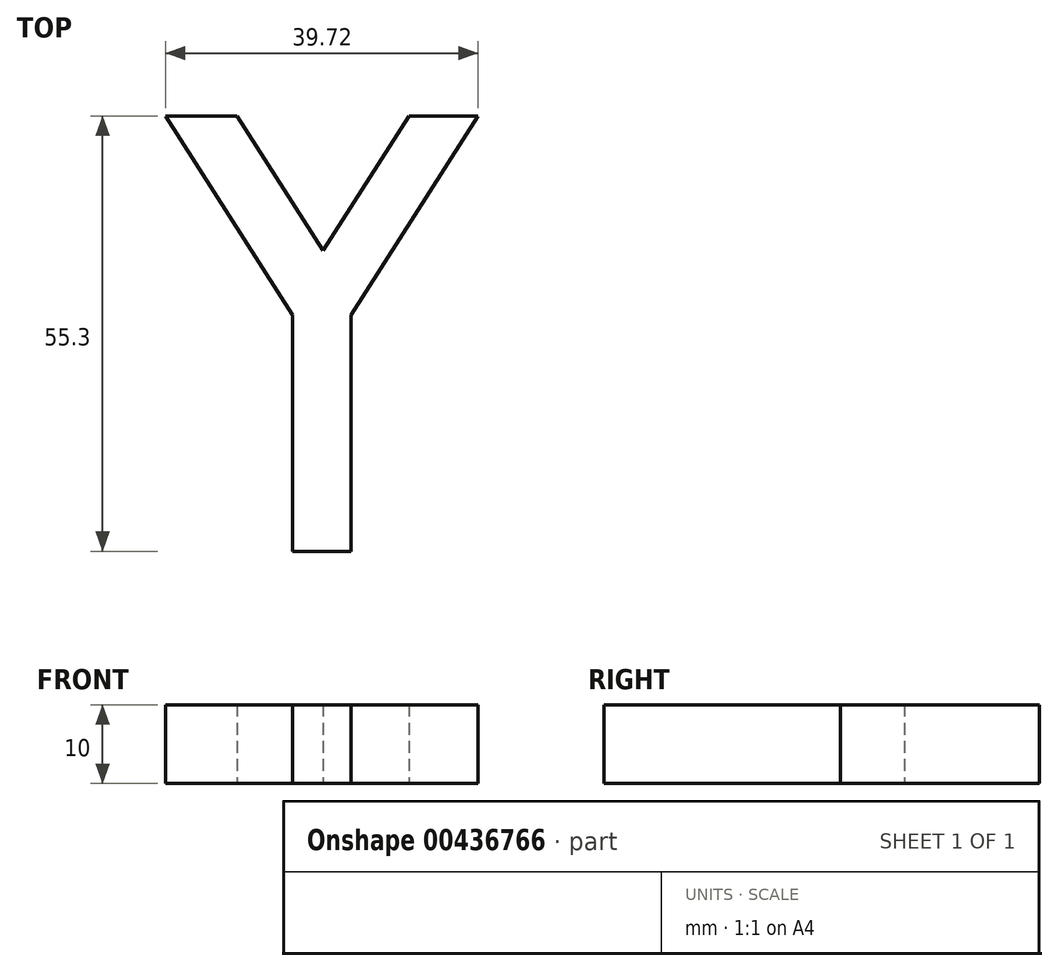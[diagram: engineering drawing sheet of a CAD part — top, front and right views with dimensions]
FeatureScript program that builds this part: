
annotation { "Feature Type Name" : "Feature", "Feature Type Description" : "" }
export const myFeature = defineFeature(function(context is Context, id is Id, definition is map)
    precondition{}
    {
        {
            var Q0;
            Q0=qCreatedBy(makeId("Top.planeOp"),FACE);
            var sketch = newSketch(context, id + "F0", { "sketchPlane" : qUnion([Q0])});
            skLineSegment(sketch, "E0", {"start": v(18.43, 27.61) * mm, "end": v(18.43, -2.39) * mm});
            skLineSegment(sketch, "E1", {"start": v(18.43, 27.61) * mm, "end": v(34.55, 52.91) * mm});
            skLineSegment(sketch, "E2", {"start": v(34.55, 52.91) * mm, "end": v(38.29, 52.91) * mm});
            skLineSegment(sketch, "E3", {"start": v(38.29, 52.91) * mm, "end": v(22.16, 27.61) * mm});
            skLineSegment(sketch, "E4", {"start": v(22.16, -2.39) * mm, "end": v(18.43, -2.39) * mm});
            skLineSegment(sketch, "E5", {"start": v(22.16, 27.61) * mm, "end": v(22.16, -2.39) * mm});
            skLineSegment(sketch, "E6.MirrorCS", {"start": v(18.43, 27.61) * mm, "end": v(2.3, 52.91) * mm});
            skLineSegment(sketch, "E7.MirrorCS", {"start": v(-1.43, 52.91) * mm, "end": v(14.7, 27.61) * mm});
            skLineSegment(sketch, "E8.MirrorCS", {"start": v(14.7, 27.61) * mm, "end": v(14.7, -2.39) * mm});
            skLineSegment(sketch, "E9.MirrorCS", {"start": v(14.7, -2.39) * mm, "end": v(18.43, -2.39) * mm});
            skLineSegment(sketch, "E10.MirrorCS", {"start": v(2.3, 52.91) * mm, "end": v(-1.43, 52.91) * mm});
            skLineSegment(sketch, "E11", {"start": v(2.3, 52.91) * mm, "end": v(7.69, 52.91) * mm});
            skLineSegment(sketch, "E12", {"start": v(7.69, 52.91) * mm, "end": v(21.12, 31.84) * mm});
            skLineSegment(sketch, "E13", {"start": v(21.12, 31.84) * mm, "end": v(34.55, 52.91) * mm});
            skLineSegment(sketch, "E14", {"start": v(34.55, 52.91) * mm, "end": v(29.52, 52.91) * mm});
            skLineSegment(sketch, "E15", {"start": v(29.52, 52.91) * mm, "end": v(18.43, 35.51) * mm});
            skSolve(sketch);
        }
        {
            var Q0;
            Q0 = qSketchRegion(id + "F0", true);
            extrude(context, id + "F1", {"entities" : qUnion([Q0]), "depth" : 10 * mm});
        }
    });
